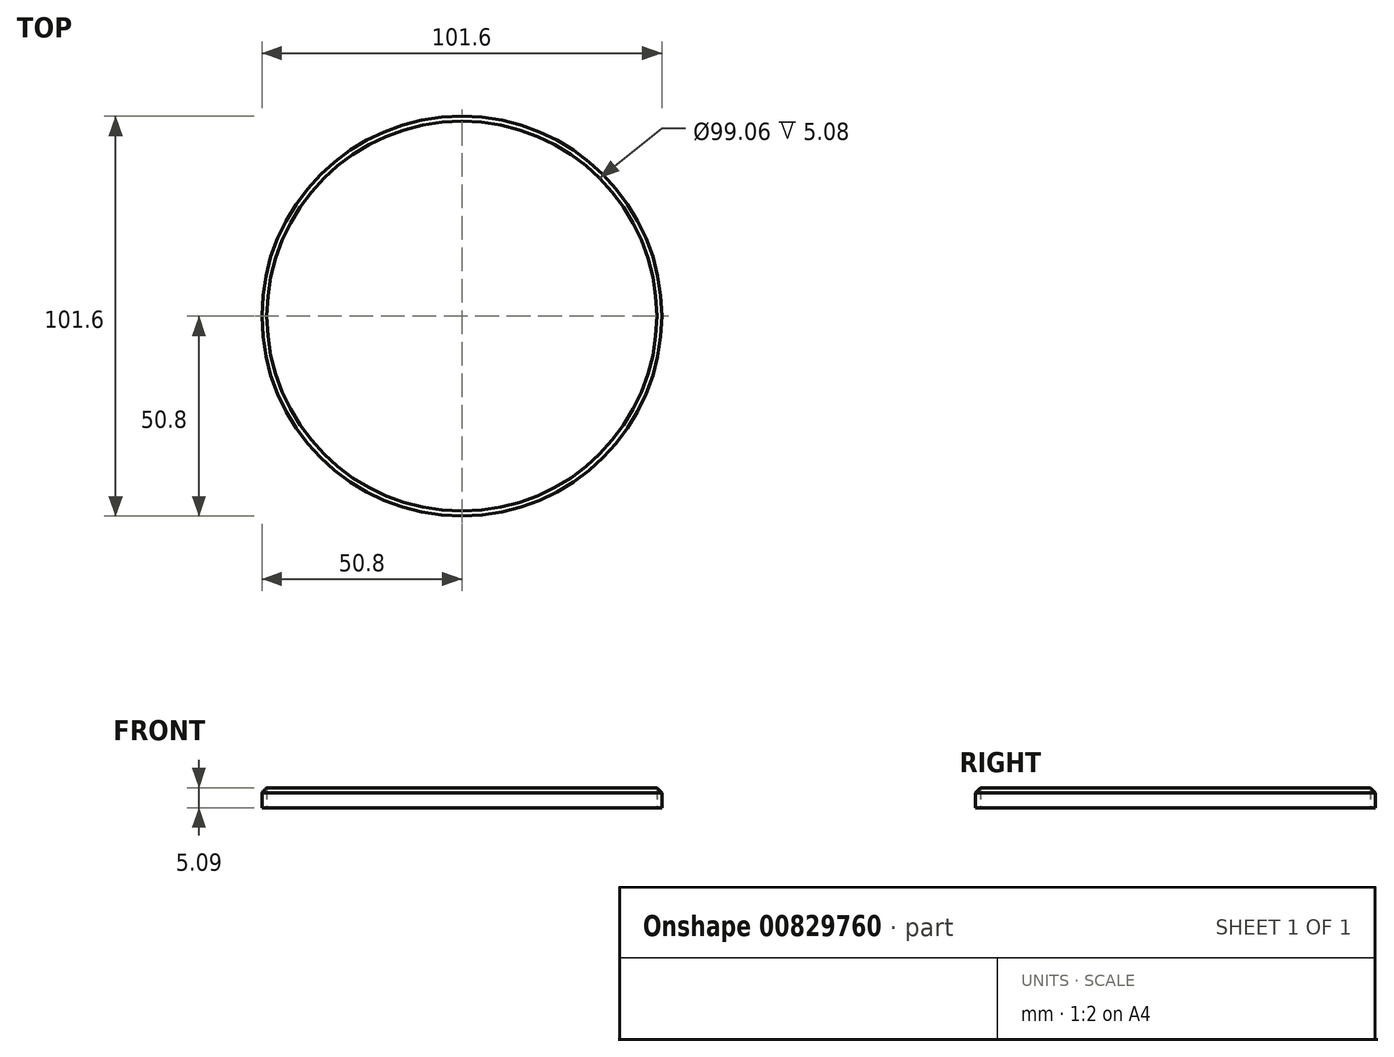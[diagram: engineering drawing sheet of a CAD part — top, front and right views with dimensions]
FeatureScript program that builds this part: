
annotation { "Feature Type Name" : "Feature", "Feature Type Description" : "" }
export const myFeature = defineFeature(function(context is Context, id is Id, definition is map)
    precondition{}
    {
        {
            var Q0;
            Q0=qCreatedBy(makeId("Top.planeOp"),FACE);
            var sketch = newSketch(context, id + "F0", { "sketchPlane" : qUnion([Q0])});
            skCircle(sketch, "E0", {"center": v(0, 0) * mm, "radius": 50.8 * mm});
            skCircle(sketch, "E1", {"center": v(0, 0) * mm, "radius": 49.53 * mm});
            skSolve(sketch);
        }
        {
            var Q0;
            Q0=makeQuery(id+"F0.imprint","IMPRINT",FACE,{"disambiguationData":[TD([[makeQuery(id+"F0.imprint","IMPRINT",EDGE,{"derivedFrom":sQuery(id+"F0.wireOp",EDGE,"E0")}),1.0]])]});
            extrude(context, id + "F1", {"entities" : qUnion([Q0]), "endBound" : BoundingType.SYMMETRIC, "depth" : 6.35 * mm, "offsetDistance" : 25.4 * mm});
        }
        {
            var Q0;
            Q0=makeQuery(id+"F1.opExtrude","CAP_EDGE",EDGE,{"disambiguationData":[OSD([sQuery(id+"F0.wireOp",EDGE,"E0")])],"isStart":false});
            chamfer(context, id + "F2", {"entities" : qUnion([Q0]), "width" : 2.54 * mm, "tangentPropagation" : true});
        }
    });
